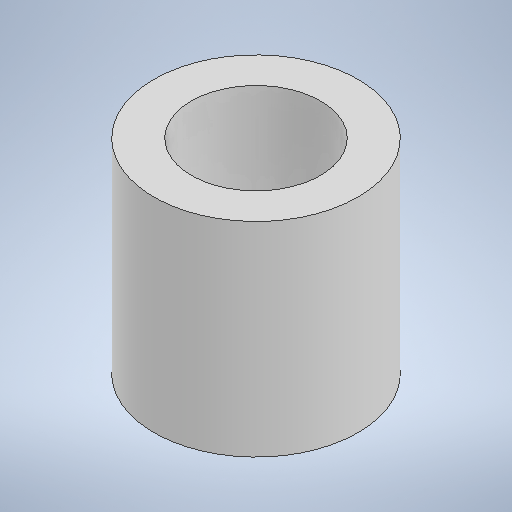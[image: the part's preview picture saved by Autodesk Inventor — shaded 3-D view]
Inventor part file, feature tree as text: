
AUTODESK INVENTOR PART (.ipt)
format: ipt  version: 2025.1 (Build 291241000, 241)  size: 505,856 bytes
history: native  units: in
note: dims shown in document units (in); Inventor stores cm internally (conversion verified against a paired STEP export)
features: extrude x1, sketch x1
ambient origin geometry x8: Origin, YZ Plane, XZ Plane, XY Plane, X Axis, Y Axis, Z Axis, Center Point
bodies: Solid1 (feature_tree)
feature tree (2):
  extrude  "Extrusion1"  Depth=0.1929in
  sketch  "Sketch1"  dims[d0=0.122in d1=0.1929in d2=0.1929in d3=0.0in]
